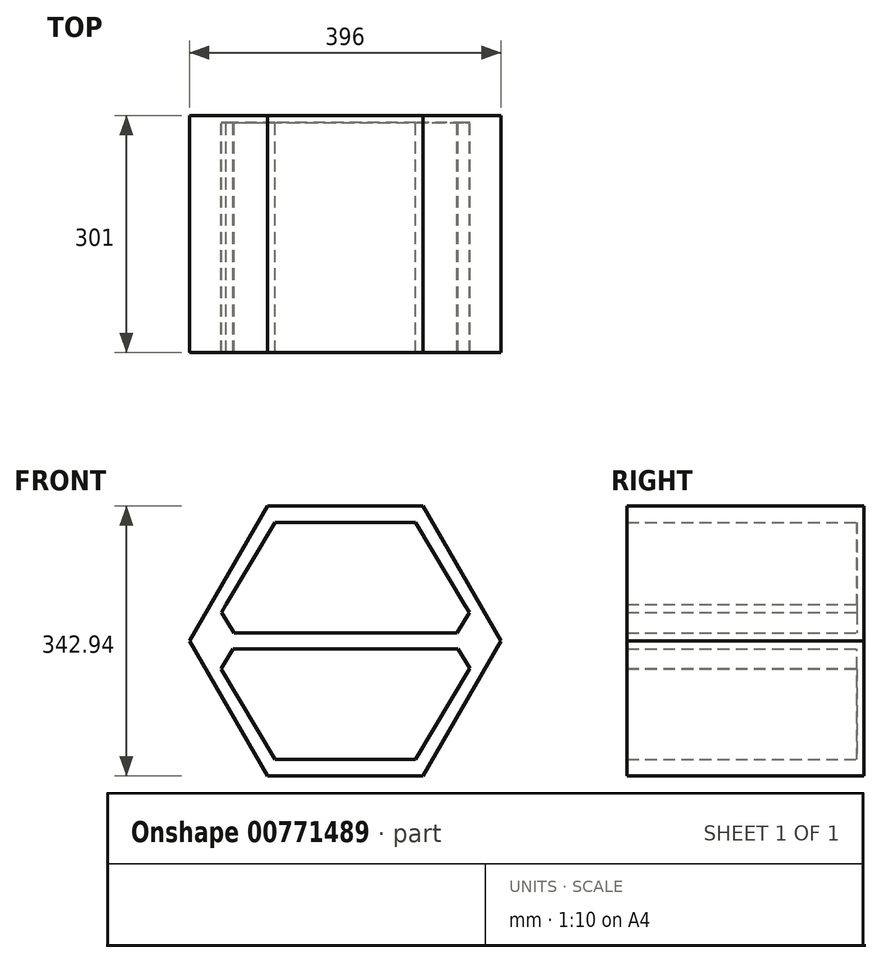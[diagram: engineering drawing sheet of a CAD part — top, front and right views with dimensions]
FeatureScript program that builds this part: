
annotation { "Feature Type Name" : "Feature", "Feature Type Description" : "" }
export const myFeature = defineFeature(function(context is Context, id is Id, definition is map)
    precondition{}
    {
        {
            var Q0;
            Q0=qCreatedBy(makeId("Front.planeOp"),FACE);
            var sketch = newSketch(context, id + "F0", { "sketchPlane" : qUnion([Q0])});
            skLineSegment(sketch, "E0", {"start": v(-303, 171.47) * mm, "end": v(-402, 0) * mm});
            skLineSegment(sketch, "E1", {"start": v(-402, 0) * mm, "end": v(-303, -171.47) * mm});
            skLineSegment(sketch, "E2", {"start": v(-303, -171.47) * mm, "end": v(-105, -171.47) * mm});
            skLineSegment(sketch, "E3", {"start": v(-105, -171.47) * mm, "end": v(-6, 0) * mm});
            skLineSegment(sketch, "E4", {"start": v(-6, 0) * mm, "end": v(-105, 171.47) * mm});
            skLineSegment(sketch, "E5", {"start": v(-105, 171.47) * mm, "end": v(-303, 171.47) * mm});
            skLineSegment(sketch, "E6", {"start": v(-361.78, -35.74) * mm, "end": v(-293.5, -150.74) * mm});
            skLineSegment(sketch, "E7", {"start": v(-293.5, -150.74) * mm, "end": v(-114.5, -150.74) * mm});
            skLineSegment(sketch, "E8", {"start": v(-114.5, -150.74) * mm, "end": v(-46.27, -35.82) * mm});
            skLineSegment(sketch, "E9", {"start": v(-51.65, 44.89) * mm, "end": v(-114.5, 150.74) * mm});
            skLineSegment(sketch, "E10", {"start": v(-114.5, 150.74) * mm, "end": v(-293.5, 150.74) * mm});
            skLineSegment(sketch, "E11", {"start": v(-293.5, 150.74) * mm, "end": v(-355.36, 46.56) * mm});
            skLineSegment(sketch, "E12", {"start": v(-355.36, 46.56) * mm, "end": v(-361.19, 36.37) * mm});
            skLineSegment(sketch, "E13", {"start": v(-51.65, 44.89) * mm, "end": v(-46.41, 36.17) * mm});
            skLineSegment(sketch, "E14", {"start": v(-46.27, -35.82) * mm, "end": v(-45.8, -35) * mm});
            skLineSegment(sketch, "E15", {"start": v(-361.78, -35.74) * mm, "end": v(-361.95, -35.44) * mm});
            skLineSegment(sketch, "E16", {"start": v(-361.19, 36.37) * mm, "end": v(-345.53, 10) * mm});
            skLineSegment(sketch, "E17", {"start": v(-97.7, 122.45) * mm, "end": v(-97.27, 123.18) * mm});
            skLineSegment(sketch, "E18", {"start": v(-345.53, 10) * mm, "end": v(-61.95, 10) * mm});
            skLineSegment(sketch, "E19", {"start": v(-346.84, -10) * mm, "end": v(-60.64, -10) * mm});
            skLineSegment(sketch, "E20", {"start": v(-361.95, -35.44) * mm, "end": v(-346.84, -10) * mm});
            skLineSegment(sketch, "E21", {"start": v(-46.41, 36.17) * mm, "end": v(-61.95, 10) * mm});
            skLineSegment(sketch, "E22", {"start": v(-45.8, -35) * mm, "end": v(-60.64, -10) * mm});
            skSolve(sketch);
        }
        {
            var Q0;
            Q0=makeQuery(id+"F0.imprint","IMPRINT",FACE,{"disambiguationData":[TD([[makeQuery(id+"F0.imprint","IMPRINT",EDGE,{"derivedFrom":sQuery(id+"F0.wireOp",EDGE,"E0")}),1.0]])]});
            extrude(context, id + "F1", {"entities" : qUnion([Q0]), "depth" : 292 * mm, "offsetDistance" : 25 * mm});
        }
        {
            var Q0;
            Q0=makeQuery(id+"F0.imprint","IMPRINT",FACE,{"disambiguationData":[TD([[makeQuery(id+"F0.imprint","IMPRINT",EDGE,{"derivedFrom":sQuery(id+"F0.wireOp",EDGE,"E6")}),1.0]])]});
            var Q1;
            {var subQ0=sQuery(id+"F0.wireOp",EDGE,"E10");Q1=makeQuery(id+"F0.imprint","IMPRINT",FACE,{"disambiguationData":[TD([[makeQuery(id+"F0.imprint","IMPRINT",EDGE,{"derivedFrom":subQ0}),1.0]])]});}
            var Q2;
            Q2=makeQuery(id+"F0.imprint","IMPRINT",FACE,{"disambiguationData":[TD([[makeQuery(id+"F0.imprint","IMPRINT",EDGE,{"derivedFrom":sQuery(id+"F0.wireOp",EDGE,"E0")}),1.0]])]});
            extrude(context, id + "F2", {"entities" : qUnion([Q0, Q1, Q2]), "operationType" : NewBodyOperationType.ADD, "oppositeDirection" : true, "depth" : 9 * mm, "offsetDistance" : 25 * mm});
        }
    });
